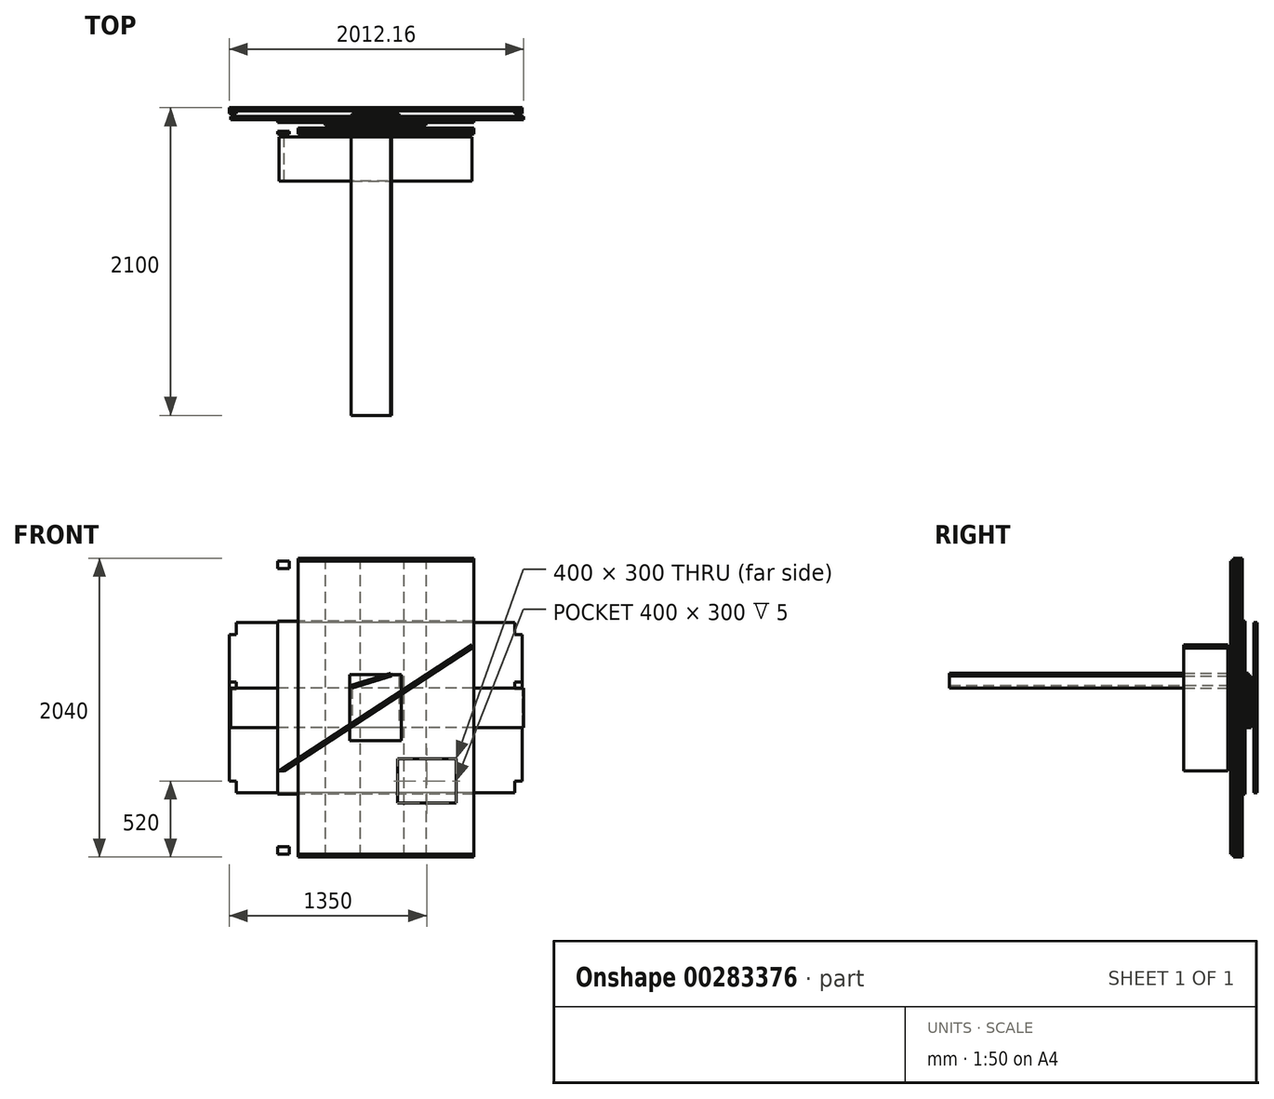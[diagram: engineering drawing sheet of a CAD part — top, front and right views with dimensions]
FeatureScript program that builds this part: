
annotation { "Feature Type Name" : "Feature", "Feature Type Description" : "" }
export const myFeature = defineFeature(function(context is Context, id is Id, definition is map)
    precondition{}
    {
        {
            var Q0;
            Q0=qCreatedBy(makeId("Front.planeOp"),FACE);
            var sketch = newSketch(context, id + "F0", { "sketchPlane" : qUnion([Q0])});
            skLineSegment(sketch, "E0.bottom", {"start": v(1000, 580) * mm, "end": v(-1000, 580) * mm});
            skLineSegment(sketch, "E0.top", {"start": v(1000, -580) * mm, "end": v(-1000, -580) * mm});
            skLineSegment(sketch, "E0.left", {"start": v(1000, 580) * mm, "end": v(1000, -580) * mm});
            skLineSegment(sketch, "E0.right", {"start": v(-1000, 580) * mm, "end": v(-1000, -580) * mm});
            skPoint(sketch, "E0.middle", {"position": v(0, 0) * mm});
            skLineSegment(sketch, "E1.bottom", {"start": v(-1000, 580) * mm, "end": v(-950, 580) * mm});
            skLineSegment(sketch, "E1.top", {"start": v(-1000, 500) * mm, "end": v(-950, 500) * mm});
            skLineSegment(sketch, "E1.left", {"start": v(-1000, 580) * mm, "end": v(-1000, 500) * mm});
            skLineSegment(sketch, "E1.right", {"start": v(-950, 580) * mm, "end": v(-950, 500) * mm});
            skLineSegment(sketch, "E2.bottom", {"start": v(1000, 580) * mm, "end": v(950, 580) * mm});
            skLineSegment(sketch, "E2.top", {"start": v(1000, 500) * mm, "end": v(950, 500) * mm});
            skLineSegment(sketch, "E2.left", {"start": v(1000, 580) * mm, "end": v(1000, 500) * mm});
            skLineSegment(sketch, "E2.right", {"start": v(950, 580) * mm, "end": v(950, 500) * mm});
            skLineSegment(sketch, "E3.bottom", {"start": v(1000, -580) * mm, "end": v(950, -580) * mm});
            skLineSegment(sketch, "E3.top", {"start": v(1000, -500) * mm, "end": v(950, -500) * mm});
            skLineSegment(sketch, "E3.left", {"start": v(1000, -580) * mm, "end": v(1000, -500) * mm});
            skLineSegment(sketch, "E3.right", {"start": v(950, -580) * mm, "end": v(950, -500) * mm});
            skLineSegment(sketch, "E4.bottom", {"start": v(-1000, -580) * mm, "end": v(-950, -580) * mm});
            skLineSegment(sketch, "E4.top", {"start": v(-1000, -500) * mm, "end": v(-950, -500) * mm});
            skLineSegment(sketch, "E4.left", {"start": v(-1000, -580) * mm, "end": v(-1000, -500) * mm});
            skLineSegment(sketch, "E4.right", {"start": v(-950, -580) * mm, "end": v(-950, -500) * mm});
            skSolve(sketch);
        }
        {
            var Q0;
            {var subQ3=sQuery(id+"F0.wireOp",EDGE,"E1.top");Q0=makeQuery(id+"F0.imprint","IMPRINT",FACE,{"disambiguationData":[TD([[makeQuery(id+"F0.imprint","IMPRINT",EDGE,{"derivedFrom":subQ3}),-1.0]])]});}
            extrude(context, id + "F1", {"entities" : qUnion([Q0]), "depth" : 20 * mm});
        }
        {
            var Q0;
            Q0=makeQuery(id+"F1.opExtrude","CAP_FACE",FACE,{"disambiguationData":[OSD([sQuery(id+"F0.wireOp",EDGE,"E0.bottom"),sQuery(id+"F0.wireOp",EDGE,"E0.top"),sQuery(id+"F0.wireOp",EDGE,"E0.left"),sQuery(id+"F0.wireOp",EDGE,"E0.right"),sQuery(id+"F0.wireOp",EDGE,"E1.top"),sQuery(id+"F0.wireOp",EDGE,"E1.right"),sQuery(id+"F0.wireOp",EDGE,"E2.top"),sQuery(id+"F0.wireOp",EDGE,"E2.right"),sQuery(id+"F0.wireOp",EDGE,"E3.top"),sQuery(id+"F0.wireOp",EDGE,"E3.right"),sQuery(id+"F0.wireOp",EDGE,"E4.top"),sQuery(id+"F0.wireOp",EDGE,"E4.right")])],"isStart":false});
            var sketch = newSketch(context, id + "F2", { "sketchPlane" : qUnion([Q0])});
            skLineSegment(sketch, "E5.bottom", {"start": v(1000, 175) * mm, "end": v(-1000, 175) * mm});
            skLineSegment(sketch, "E5.top", {"start": v(1000, -175) * mm, "end": v(-1000, -175) * mm});
            skLineSegment(sketch, "E5.left", {"start": v(1000, 175) * mm, "end": v(1000, -175) * mm});
            skLineSegment(sketch, "E5.right", {"start": v(-1000, 175) * mm, "end": v(-1000, -175) * mm});
            skPoint(sketch, "E5.middle", {"position": v(0, 0) * mm});
            skLineSegment(sketch, "E6.bottom", {"start": v(-1000, 175) * mm, "end": v(-950, 175) * mm});
            skLineSegment(sketch, "E6.top", {"start": v(-1000, 125) * mm, "end": v(-950, 125) * mm});
            skLineSegment(sketch, "E6.left", {"start": v(-1000, 175) * mm, "end": v(-1000, 125) * mm});
            skLineSegment(sketch, "E6.right", {"start": v(-950, 175) * mm, "end": v(-950, 125) * mm});
            skLineSegment(sketch, "E7.bottom", {"start": v(1000, 175) * mm, "end": v(950, 175) * mm});
            skLineSegment(sketch, "E7.top", {"start": v(1000, 125) * mm, "end": v(950, 125) * mm});
            skLineSegment(sketch, "E7.left", {"start": v(1000, 175) * mm, "end": v(1000, 125) * mm});
            skLineSegment(sketch, "E7.right", {"start": v(950, 175) * mm, "end": v(950, 125) * mm});
            skSolve(sketch);
        }
        {
            var Q0;
            Q0=makeQuery(id+"F2.imprint","IMPRINT",FACE,{"disambiguationData":[TD([[makeQuery(id+"F2.imprint","IMPRINT",EDGE,{"derivedFrom":sQuery(id+"F2.wireOp",EDGE,"E5.bottom")}),1.0]])]});
            extrude(context, id + "F3", {"entities" : qUnion([Q0]), "depth" : 20 * mm});
        }
        {
            var Q0;
            Q0=makeQuery(id+"F3.opExtrude","CAP_FACE",FACE,{"disambiguationData":[OSD([sQuery(id+"F2.wireOp",EDGE,"E5.bottom"),sQuery(id+"F2.wireOp",EDGE,"E5.top"),sQuery(id+"F2.wireOp",EDGE,"E5.left"),sQuery(id+"F2.wireOp",EDGE,"E5.right"),sQuery(id+"F2.wireOp",EDGE,"E6.top"),sQuery(id+"F2.wireOp",EDGE,"E6.right"),sQuery(id+"F2.wireOp",EDGE,"E7.top"),sQuery(id+"F2.wireOp",EDGE,"E7.right")])],"isStart":false});
            var sketch = newSketch(context, id + "F4", { "sketchPlane" : qUnion([Q0])});
            skLineSegment(sketch, "E8.bottom", {"start": v(160, 135) * mm, "end": v(-160, 135) * mm});
            skLineSegment(sketch, "E8.top", {"start": v(160, -135) * mm, "end": v(-160, -135) * mm});
            skLineSegment(sketch, "E8.left", {"start": v(160, 135) * mm, "end": v(160, -135) * mm});
            skLineSegment(sketch, "E8.right", {"start": v(-160, 135) * mm, "end": v(-160, -135) * mm});
            skPoint(sketch, "E8.middle", {"position": v(0, 0) * mm});
            skLineSegment(sketch, "E9", {"start": v(160, 135) * mm, "end": v(160, 215) * mm});
            skLineSegment(sketch, "E10", {"start": v(160, 215) * mm, "end": v(110, 215) * mm});
            skLineSegment(sketch, "E11", {"start": v(110, 215) * mm, "end": v(-160, 135) * mm});
            skSolve(sketch);
        }
        {
            var Q0;
            Q0 = qSketchRegion(id + "F4", true);
            extrude(context, id + "F5", {"entities" : qUnion([Q0]), "depth" : 20 * mm});
        }
        {
            var Q0;
            Q0=makeQuery(id+"F5.opExtrude","CAP_FACE",FACE,{"disambiguationData":[OSD([sQuery(id+"F4.wireOp",EDGE,"E8.top"),sQuery(id+"F4.wireOp",EDGE,"E8.left"),sQuery(id+"F4.wireOp",EDGE,"E8.right"),sQuery(id+"F4.wireOp",EDGE,"E9"),sQuery(id+"F4.wireOp",EDGE,"DMPNzLVu-4za3-Tgjm-qbeb-1pcYbcp1HCBX")])],"isStart":false});
            var sketch = newSketch(context, id + "F6", { "sketchPlane" : qUnion([Q0])});
            skLineSegment(sketch, "E12.bottom", {"start": v(1012.16, 135) * mm, "end": v(-987.84, 135) * mm});
            skLineSegment(sketch, "E12.top", {"start": v(1012.16, -135) * mm, "end": v(-987.84, -135) * mm});
            skLineSegment(sketch, "E12.left", {"start": v(1012.16, 135) * mm, "end": v(1012.16, -135) * mm});
            skLineSegment(sketch, "E12.right", {"start": v(-987.84, 135) * mm, "end": v(-987.84, -135) * mm});
            skPoint(sketch, "E12.middle", {"position": v(12.16, 0) * mm});
            skSolve(sketch);
        }
        {
            var Q0;
            Q0 = qSketchRegion(id + "F6", true);
            extrude(context, id + "F7", {"entities" : qUnion([Q0]), "depth" : 20 * mm});
        }
        {
            var Q0;
            Q0=makeQuery(id+"F5.opExtrude","CAP_FACE",FACE,{"disambiguationData":[OSD([sQuery(id+"F4.wireOp",EDGE,"E8.top"),sQuery(id+"F4.wireOp",EDGE,"E8.left"),sQuery(id+"F4.wireOp",EDGE,"E8.right"),sQuery(id+"F4.wireOp",EDGE,"E9"),sQuery(id+"F4.wireOp",EDGE,"E10"),sQuery(id+"F4.wireOp",EDGE,"E11")])],"isStart":false});
            var sketch = newSketch(context, id + "F8", { "sketchPlane" : qUnion([Q0])});
            skLineSegment(sketch, "E13.0", {"start": v(110, 215) * mm, "end": v(-160, 135) * mm});
            skLineSegment(sketch, "E14", {"start": v(-160, 135) * mm, "end": v(-165.68, 154.18) * mm});
            skLineSegment(sketch, "E15", {"start": v(-165.68, 154.18) * mm, "end": v(104.32, 234.18) * mm});
            skLineSegment(sketch, "E16", {"start": v(104.32, 234.18) * mm, "end": v(110, 215) * mm});
            skSolve(sketch);
        }
        {
            var Q0;
            Q0 = qSketchRegion(id + "F8", true);
            extrude(context, id + "F9", {"entities" : qUnion([Q0]), "depth" : 2040 * mm});
        }
        {
            var Q0;
            Q0=makeQuery(id+"F7.opExtrude","CAP_FACE",FACE,{"disambiguationData":[OSD([sQuery(id+"F6.wireOp",EDGE,"E12.bottom"),sQuery(id+"F6.wireOp",EDGE,"E12.top"),sQuery(id+"F6.wireOp",EDGE,"E12.left"),sQuery(id+"F6.wireOp",EDGE,"E12.right")])],"isStart":false});
            var sketch = newSketch(context, id + "F10", { "sketchPlane" : qUnion([Q0])});
            skLineSegment(sketch, "E17.bottom", {"start": v(670, 590) * mm, "end": v(-670, 590) * mm});
            skLineSegment(sketch, "E17.top", {"start": v(670, -590) * mm, "end": v(-670, -590) * mm});
            skLineSegment(sketch, "E17.left", {"start": v(670, 590) * mm, "end": v(670, -590) * mm});
            skLineSegment(sketch, "E17.right", {"start": v(-670, 590) * mm, "end": v(-670, -590) * mm});
            skPoint(sketch, "E17.middle", {"position": v(0, 0) * mm});
            skSolve(sketch);
        }
        {
            var Q0;
            Q0 = qSketchRegion(id + "F10", true);
            extrude(context, id + "F11", {"entities" : qUnion([Q0]), "depth" : 20 * mm});
        }
        {
            var Q0;
            Q0=makeQuery(id+"F11.opExtrude","CAP_FACE",FACE,{"disambiguationData":[OSD([sQuery(id+"F10.wireOp",EDGE,"E17.bottom"),sQuery(id+"F10.wireOp",EDGE,"E17.top"),sQuery(id+"F10.wireOp",EDGE,"E17.left"),sQuery(id+"F10.wireOp",EDGE,"E17.right")])],"isStart":false});
            var sketch = newSketch(context, id + "F12", { "sketchPlane" : qUnion([Q0])});
            skLineSegment(sketch, "E18.bottom", {"start": v(345, 1020) * mm, "end": v(-345, 1020) * mm});
            skLineSegment(sketch, "E18.top", {"start": v(345, -1020) * mm, "end": v(-345, -1020) * mm});
            skLineSegment(sketch, "E18.left", {"start": v(345, 1020) * mm, "end": v(345, -1020) * mm});
            skLineSegment(sketch, "E18.right", {"start": v(-345, 1020) * mm, "end": v(-345, -1020) * mm});
            skPoint(sketch, "E18.middle", {"position": v(0, 0) * mm});
            skSolve(sketch);
        }
        {
            var Q0;
            Q0 = qSketchRegion(id + "F12", true);
            extrude(context, id + "F13", {"entities" : qUnion([Q0]), "depth" : 20 * mm});
        }
        {
            var Q0;
            Q0=makeQuery(id+"F13.opExtrude","CAP_FACE",FACE,{"disambiguationData":[OSD([sQuery(id+"F12.wireOp",EDGE,"E18.bottom"),sQuery(id+"F12.wireOp",EDGE,"E18.top"),sQuery(id+"F12.wireOp",EDGE,"E18.left"),sQuery(id+"F12.wireOp",EDGE,"E18.right")])],"isStart":false});
            var sketch = newSketch(context, id + "F14", { "sketchPlane" : qUnion([Q0])});
            skLineSegment(sketch, "E19.bottom", {"start": v(-106.71, 1020) * mm, "end": v(193.29, 1020) * mm});
            skLineSegment(sketch, "E19.top", {"start": v(-106.71, -1020) * mm, "end": v(193.29, -1020) * mm});
            skLineSegment(sketch, "E19.left", {"start": v(-106.71, 1020) * mm, "end": v(-106.71, -1020) * mm});
            skLineSegment(sketch, "E19.right", {"start": v(193.29, 1020) * mm, "end": v(193.29, -1020) * mm});
            skPoint(sketch, "E19.middle", {"position": v(43.29, 0) * mm});
            skSolve(sketch);
        }
        {
            var Q0;
            Q0 = qSketchRegion(id + "F14", true);
            extrude(context, id + "F15", {"entities" : qUnion([Q0]), "depth" : 20 * mm});
        }
        {
            var Q0;
            Q0=makeQuery(id+"F15.opExtrude","CAP_FACE",FACE,{"disambiguationData":[OSD([sQuery(id+"F14.wireOp",EDGE,"E19.bottom"),sQuery(id+"F14.wireOp",EDGE,"E19.top"),sQuery(id+"F14.wireOp",EDGE,"E19.left"),sQuery(id+"F14.wireOp",EDGE,"E19.right")])],"isStart":false});
            var sketch = newSketch(context, id + "F16", { "sketchPlane" : qUnion([Q0])});
            skLineSegment(sketch, "E20.bottom", {"start": v(-530.3, 1020) * mm, "end": v(669.7, 1020) * mm});
            skLineSegment(sketch, "E20.top", {"start": v(-530.3, -1020) * mm, "end": v(669.7, -1020) * mm});
            skLineSegment(sketch, "E20.left", {"start": v(-530.3, 1020) * mm, "end": v(-530.3, -1020) * mm});
            skLineSegment(sketch, "E20.right", {"start": v(669.7, 1020) * mm, "end": v(669.7, -1020) * mm});
            skPoint(sketch, "E20.middle", {"position": v(69.7, 0) * mm});
            skSolve(sketch);
        }
        {
            var Q0;
            Q0 = qSketchRegion(id + "F16", true);
            extrude(context, id + "F17", {"entities" : qUnion([Q0]), "depth" : 20 * mm});
        }
        {
            var Q0;
            Q0=makeQuery(id+"F17.opExtrude","CAP_FACE",FACE,{"disambiguationData":[OSD([sQuery(id+"F16.wireOp",EDGE,"E20.bottom"),sQuery(id+"F16.wireOp",EDGE,"E20.top"),sQuery(id+"F16.wireOp",EDGE,"E20.left"),sQuery(id+"F16.wireOp",EDGE,"E20.right")])],"isStart":false});
            var sketch = newSketch(context, id + "F18", { "sketchPlane" : qUnion([Q0])});
            skLineSegment(sketch, "E21.bottom", {"start": v(-670, 1000) * mm, "end": v(670, 1000) * mm});
            skLineSegment(sketch, "E21.top", {"start": v(-670, -1000) * mm, "end": v(670, -1000) * mm});
            skLineSegment(sketch, "E21.left", {"start": v(-670, 1000) * mm, "end": v(-670, -1000) * mm});
            skLineSegment(sketch, "E21.right", {"start": v(670, 1000) * mm, "end": v(670, -1000) * mm});
            skPoint(sketch, "E21.middle", {"position": v(0, 0) * mm});
            skLineSegment(sketch, "E22.bottom", {"start": v(-670, -1000) * mm, "end": v(-590, -1000) * mm});
            skLineSegment(sketch, "E22.top", {"start": v(-670, -950) * mm, "end": v(-590, -950) * mm});
            skLineSegment(sketch, "E22.left", {"start": v(-670, -1000) * mm, "end": v(-670, -950) * mm});
            skLineSegment(sketch, "E22.right", {"start": v(-590, -1000) * mm, "end": v(-590, -950) * mm});
            skLineSegment(sketch, "E23.bottom", {"start": v(-670, 1000) * mm, "end": v(-590, 1000) * mm});
            skLineSegment(sketch, "E23.top", {"start": v(-670, 950) * mm, "end": v(-590, 950) * mm});
            skLineSegment(sketch, "E23.left", {"start": v(-670, 1000) * mm, "end": v(-670, 950) * mm});
            skLineSegment(sketch, "E23.right", {"start": v(-590, 1000) * mm, "end": v(-590, 950) * mm});
            skSolve(sketch);
        }
        {
            var Q0;
            {var subQ0=sQuery(id+"F18.wireOp",EDGE,"E21.right");Q0=makeQuery(id+"F18.imprint","IMPRINT",FACE,{"disambiguationData":[TD([[makeQuery(id+"F18.imprint","IMPRINT",EDGE,{"derivedFrom":subQ0}),-1.0]])]});}
            var Q1;
            Q1=makeQuery(id+"F18.imprint","IMPRINT",FACE,{"disambiguationData":[TD([[makeQuery(id+"F18.imprint","IMPRINT",EDGE,{"derivedFrom":sQuery(id+"F18.wireOp",EDGE,"E21.left")}),1.0]])]});
            var Q2;
            {var subQ0=sQuery(id+"F18.wireOp",EDGE,"E21.bottom");var subQ1=makeQuery(id+"F17.opExtrude","CAP_EDGE",EDGE,{"disambiguationData":[OSD([sQuery(id+"F16.wireOp",EDGE,"E20.left")])],"isStart":false});var subQ2=makeQuery(id+"F18.imprint","INTERSECT",VERTEX,{"derivedFrom":[subQ1,subQ0]});Q2=makeQuery(id+"F18.imprint","IMPRINT",FACE,{"disambiguationData":[TD([[makeQuery(id+"F18.imprint","IMPRINT",EDGE,{"disambiguationData":[TD([[subQ2,-1.0]])],"derivedFrom":subQ0}),-1.0]])]});}
            extrude(context, id + "F19", {"entities" : qUnion([Q0, Q1, Q2]), "depth" : 20 * mm});
        }
        {
            var Q0;
            Q0=makeQuery(id+"F19.opExtrude","CAP_FACE",FACE,{"disambiguationData":[OSD([sQuery(id+"F18.wireOp",EDGE,"E21.bottom"),sQuery(id+"F18.wireOp",EDGE,"E21.top"),sQuery(id+"F18.wireOp",EDGE,"E21.left"),sQuery(id+"F18.wireOp",EDGE,"E21.right"),sQuery(id+"F18.wireOp",EDGE,"E22.top"),sQuery(id+"F18.wireOp",EDGE,"E22.right"),sQuery(id+"F18.wireOp",EDGE,"E23.top"),sQuery(id+"F18.wireOp",EDGE,"E23.right")])],"isStart":false});
            var sketch = newSketch(context, id + "F20", { "sketchPlane" : qUnion([Q0])});
            skLineSegment(sketch, "E24.bottom", {"start": v(150, -650) * mm, "end": v(550, -650) * mm});
            skLineSegment(sketch, "E24.top", {"start": v(150, -350) * mm, "end": v(550, -350) * mm});
            skLineSegment(sketch, "E24.left", {"start": v(150, -650) * mm, "end": v(150, -350) * mm});
            skLineSegment(sketch, "E24.right", {"start": v(550, -650) * mm, "end": v(550, -350) * mm});
            skSolve(sketch);
        }
        {
            var Q0;
            Q0 = qSketchRegion(id + "F20", true);
            extrude(context, id + "F21", {"entities" : qUnion([Q0]), "operationType" : NewBodyOperationType.REMOVE, "oppositeDirection" : true, "depth" : 25 * mm});
        }
        {
            var Q0;
            Q0=makeQuery(id+"F19.opExtrude","CAP_FACE",FACE,{"disambiguationData":[OSD([sQuery(id+"F18.wireOp",EDGE,"E21.bottom"),sQuery(id+"F18.wireOp",EDGE,"E21.top"),sQuery(id+"F18.wireOp",EDGE,"E21.left"),sQuery(id+"F18.wireOp",EDGE,"E21.right"),sQuery(id+"F18.wireOp",EDGE,"E22.top"),sQuery(id+"F18.wireOp",EDGE,"E22.right"),sQuery(id+"F18.wireOp",EDGE,"E23.top"),sQuery(id+"F18.wireOp",EDGE,"E23.right")])],"isStart":false});
            var sketch = newSketch(context, id + "F22", { "sketchPlane" : qUnion([Q0])});
            skLineSegment(sketch, "E25.bottom", {"start": v(175, 225) * mm, "end": v(-175, 225) * mm});
            skLineSegment(sketch, "E25.top", {"start": v(175, -225) * mm, "end": v(-175, -225) * mm});
            skLineSegment(sketch, "E25.left", {"start": v(175, 225) * mm, "end": v(175, -225) * mm});
            skLineSegment(sketch, "E25.right", {"start": v(-175, 225) * mm, "end": v(-175, -225) * mm});
            skPoint(sketch, "E25.middle", {"position": v(0, 0) * mm});
            skSolve(sketch);
        }
        {
            var Q0;
            Q0 = qSketchRegion(id + "F22", true);
            extrude(context, id + "F23", {"entities" : qUnion([Q0]), "depth" : 20 * mm});
        }
        {
            var Q0;
            Q0=makeQuery(id+"F23.opExtrude","CAP_FACE",FACE,{"disambiguationData":[OSD([sQuery(id+"F22.wireOp",EDGE,"E25.bottom"),sQuery(id+"F22.wireOp",EDGE,"E25.top"),sQuery(id+"F22.wireOp",EDGE,"E25.left"),sQuery(id+"F22.wireOp",EDGE,"E25.right")])],"isStart":false});
            var sketch = newSketch(context, id + "F24", { "sketchPlane" : qUnion([Q0])});
            skLineSegment(sketch, "E26.bottom", {"start": v(660, 430) * mm, "end": v(-660, 430) * mm, "construction": true});
            skLineSegment(sketch, "E26.top", {"start": v(660, -430) * mm, "end": v(-660, -430) * mm, "construction": true});
            skLineSegment(sketch, "E26.left", {"start": v(660, 430) * mm, "end": v(660, -430) * mm, "construction": true});
            skLineSegment(sketch, "E26.right", {"start": v(-660, 430) * mm, "end": v(-660, -430) * mm, "construction": true});
            skPoint(sketch, "E26.middle", {"position": v(0, 0) * mm});
            skLineSegment(sketch, "E27", {"start": v(-660, -430) * mm, "end": v(660, 430) * mm});
            skLineSegment(sketch, "E28", {"start": v(660, 406.13) * mm, "end": v(-623.36, -430) * mm});
            skLineSegment(sketch, "E29", {"start": v(-623.36, -430) * mm, "end": v(-660, -430) * mm, "construction": true});
            skLineSegment(sketch, "E30", {"start": v(660, 430) * mm, "end": v(660, 406.13) * mm});
            skLineSegment(sketch, "E31", {"start": v(-660, -430) * mm, "end": v(-623.36, -430) * mm});
            skSolve(sketch);
        }
        {
            var Q0;
            Q0 = qSketchRegion(id + "F24", true);
            extrude(context, id + "F25", {"entities" : qUnion([Q0]), "depth" : 300 * mm});
        }
    });
